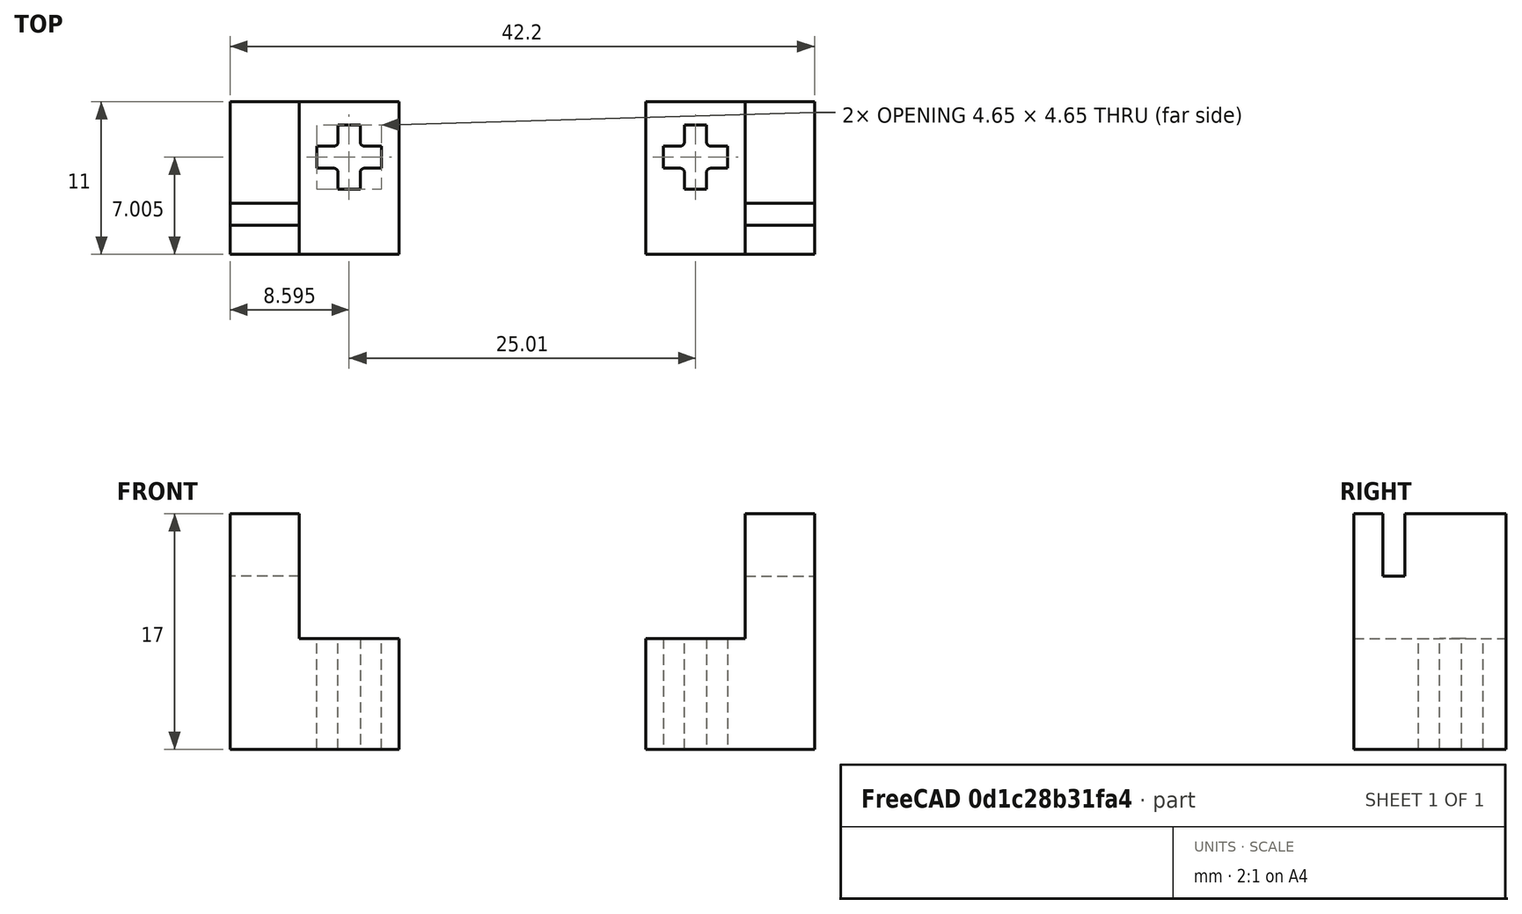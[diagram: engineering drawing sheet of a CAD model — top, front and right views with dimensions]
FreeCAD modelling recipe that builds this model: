
FCSTD DOCUMENT  (FreeCAD 0.20R29177 +426 (Git))
Label: arduinoHolder
License: All rights reserved
LicenseURL: http://en.wikipedia.org/wiki/All_rights_reserved
objects: Part::Box×7, Mesh::Feature×6, Part::MultiFuse×5, Part::Cut×2, Part::Fillet×2, Part::FeaturePython×2, App::DocumentObjectGroup×1
note: 18 computed .brp shape members not serialized (recipe doc carries the construction recipe); baked Part::Feature solids carry a one-line shape summary decoded from their .brp

FEATURE [Mesh::Feature] _2009  label="32009"
  Placement = pos=(0,0,0) rot=(0,1,0;-1.5708rad)
FEATURE [Mesh::Feature] _2010  label="32009001"
  Placement = pos=(-8,0,0) rot=(0,1,0;-1.5708rad)
FEATURE [Mesh::Feature] _2011  label="32009002"
  Placement = pos=(8,0,0) rot=(0,1,0;-1.5708rad)
FEATURE [Mesh::Feature] _2012  label="32009003"
  Placement = pos=(-16,0,0) rot=(0,1,0;-1.5708rad)
FEATURE [Mesh::Feature] _2013  label="32009004"
  Placement = pos=(16,0,0) rot=(0,1,0;-1.5708rad)
FEATURE [Part::Box] Box  label="arduino"
  AttacherType = Attacher::AttachEngine3D
  Height = 60
  Length = 31
  Placement = pos=(-15.5,-52.9,3.6) rot=(0,0,1;0rad)
  Width = 1.58
FEATURE [Mesh::Feature] _737  label="3737"
  Placement = pos=(0,-48,0) rot=(0,0,1;0rad)
FEATURE [Part::Box] Box001  label="Cube"
  AttacherType = Attacher::AttachEngine3D
  Height = 80
  Length = 1.6
  Placement = pos=(0,0,0) rot=(0,0,1;1.5708rad)
  Width = 4.65
FEATURE [Part::Box] Box002  label="Cube001"
  AttacherType = Attacher::AttachEngine3D
  Height = 80
  Length = 1.6
  Placement = pos=(-3.12,-1.52,0) rot=(0,1,0;0rad)
  Width = 4.65
FEATURE [Part::MultiFuse] Fusion
  Placement = pos=(-40,-48.8,-2.32) rot=(0,1,0;1.5708rad)
  Shapes = -> [Box001,Box002]
FEATURE [Part::Box] Box003  label="Cube002"
  AttacherType = Attacher::AttachEngine3D
  Height = 12
  Length = 8
  Placement = pos=(20,-55,-3.6) rot=(0,0,1;0rad)
  Width = 11
FEATURE [Part::Box] Box004  label="Cube003"
  AttacherType = Attacher::AttachEngine3D
  Height = 12
  Length = 8
  Placement = pos=(-28,-55,-3.6) rot=(0,0,1;0rad)
  Width = 11
FEATURE [Part::Box] Box005  label="Cube004"
  AttacherType = Attacher::AttachEngine3D
  Height = 5
  Length = 17
  Placement = pos=(11,-55,3.6) rot=(0,0,1;0rad)
  Width = 11
FEATURE [Part::Box] Box006  label="Cube005"
  AttacherType = Attacher::AttachEngine3D
  Height = 5
  Length = 17
  Placement = pos=(-28,-55,3.6) rot=(0,0,1;0rad)
  Width = 11
FEATURE [Part::MultiFuse] Fusion001
  Shapes = -> [Box003,Box005]
FEATURE [Part::MultiFuse] Fusion002
  Shapes = -> [Box004,Box006]
FEATURE [Part::MultiFuse] Fusion003
  Shapes = -> [Fusion002,Fusion001]
FEATURE [Part::Cut] Cut
  Base = -> Fusion003
  Tool = -> Fusion
FEATURE [Part::Fillet] Fillet
  Base = -> Cut
  Edges = 4 edges r=0.3: [Edge97,Edge103,Edge109,Edge115]
FEATURE [Part::Fillet] Fillet001
  Base = -> Fillet
  Edges = 4 edges r=0.3: [Edge109,Edge115,Edge121,Edge127]
FEATURE [Part::Cut] Cut001
  Base = -> Fillet001
  Tool = -> Box
FEATURE [Part::FeaturePython] Cut001_child0  label="Cut001.0"  # WARN: FeaturePython — macro-defined, semantics opaque (R4)
  Base = -> Cut001
  FilterType = 1
  Invert = false
  OverrideMaxVal = 0
  Placement = pos=(-25,0,0) rot=(0,1,0;-1.5708rad)
  WindowFrom = 80
  WindowTo = 100
  items = 0
FEATURE [Part::FeaturePython] Cut001_child1  label="Cut001.1"  # WARN: FeaturePython — macro-defined, semantics opaque (R4)
  Base = -> Cut001
  FilterType = 1
  Invert = false
  OverrideMaxVal = 0
  Placement = pos=(0,0,0) rot=(0,1,0;1.5708rad)
  WindowFrom = 80
  WindowTo = 100
  items = 1
FEATURE [Part::MultiFuse] Fusion004
  Shapes = -> [Cut001_child0,Cut001_child1]
FEATURE [App::DocumentObjectGroup] GrExplode_Cut001  label="Exploded Cut001"
  Group = -> [Fusion004]
